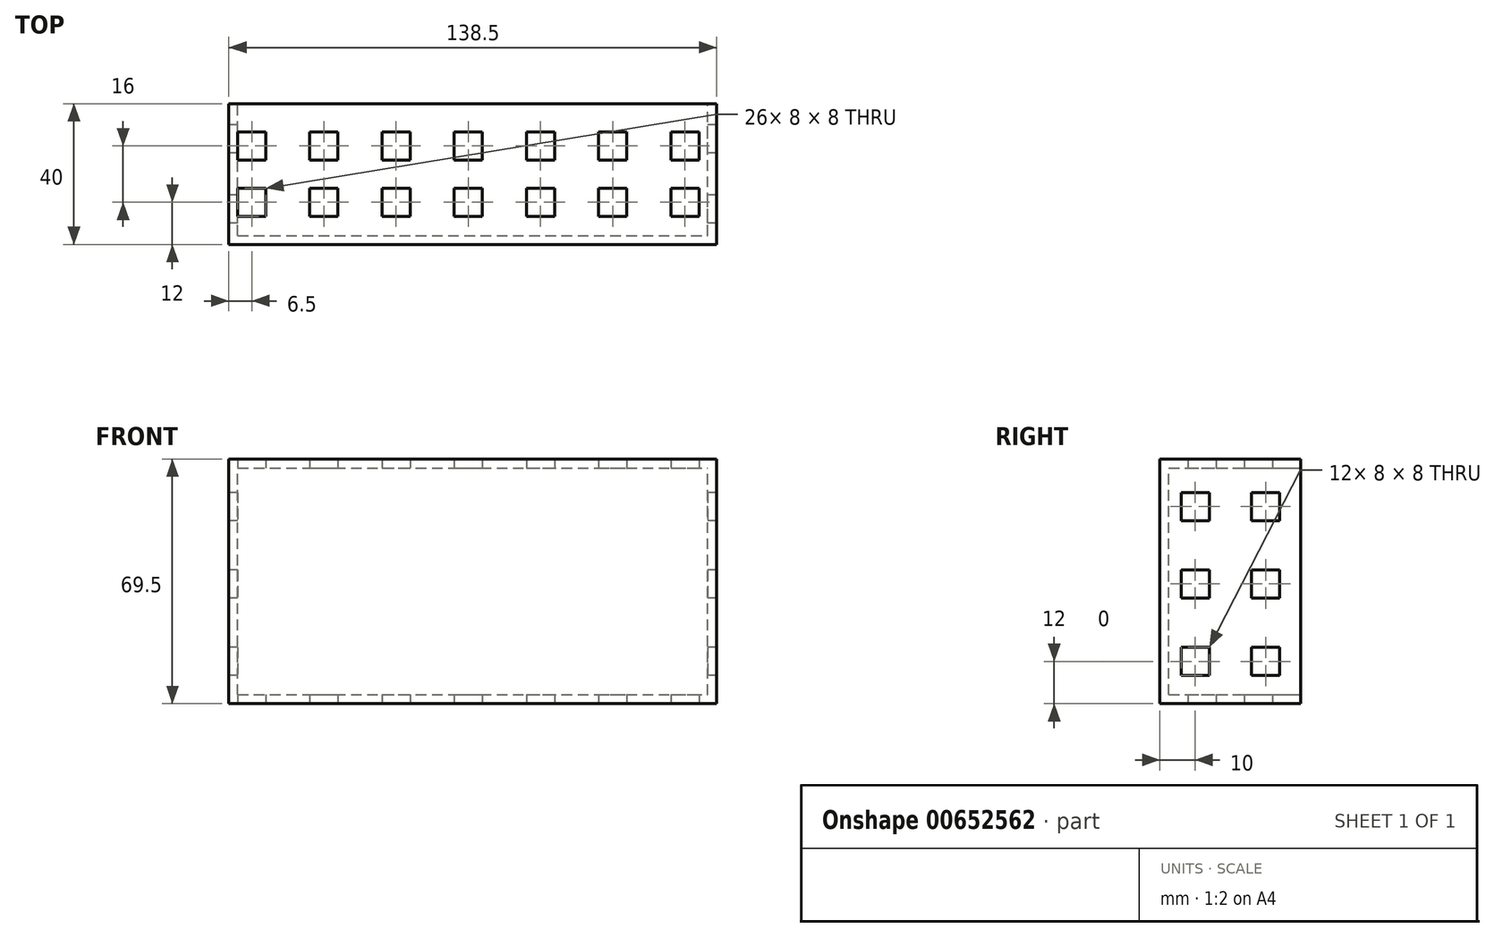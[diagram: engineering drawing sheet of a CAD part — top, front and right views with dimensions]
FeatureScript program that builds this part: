
annotation { "Feature Type Name" : "Feature", "Feature Type Description" : "" }
export const myFeature = defineFeature(function(context is Context, id is Id, definition is map)
    precondition{}
    {
        {
            var Q0;
            Q0=qCreatedBy(makeId("Front.planeOp"),FACE);
            var sketch = newSketch(context, id + "F0", { "sketchPlane" : qUnion([Q0])});
            skLineSegment(sketch, "E0.bottom", {"start": v(0, 0) * mm, "end": v(138.5, 0) * mm});
            skLineSegment(sketch, "E0.top", {"start": v(0, 69.5) * mm, "end": v(138.5, 69.5) * mm});
            skLineSegment(sketch, "E0.left", {"start": v(0, 0) * mm, "end": v(0, 69.5) * mm});
            skLineSegment(sketch, "E0.right", {"start": v(138.5, 0) * mm, "end": v(138.5, 69.5) * mm});
            skSolve(sketch);
        }
        {
            var Q0;
            Q0 = qSketchRegion(id + "F0", true);
            extrude(context, id + "F1", {"entities" : qUnion([Q0]), "depth" : 40 * mm, "offsetDistance" : 25 * mm});
        }
        {
            var Q0;
            Q0=makeQuery(id+"F1.opExtrude","CAP_FACE",FACE,{"disambiguationData":[OSD([sQuery(id+"F0.wireOp",EDGE,"E0.bottom"),sQuery(id+"F0.wireOp",EDGE,"E0.top"),sQuery(id+"F0.wireOp",EDGE,"E0.left"),sQuery(id+"F0.wireOp",EDGE,"E0.right")])],"isStart":true});
            shell(context, id + "F2", {"entities" : qUnion([Q0]), "thickness" : 2.5 * mm});
        }
        {
            var Q0;
            Q0=makeQuery(id+"F1.opExtrude","SWEPT_FACE",FACE,{"disambiguationData":[OSD([sQuery(id+"F0.wireOp",EDGE,"E0.bottom")])]});
            var sketch = newSketch(context, id + "F3", { "sketchPlane" : qUnion([Q0])});
            skLineSegment(sketch, "E1.bottom", {"start": v(10.5, 24) * mm, "end": v(2.5, 24) * mm});
            skLineSegment(sketch, "E1.top", {"start": v(10.5, 32) * mm, "end": v(2.5, 32) * mm});
            skLineSegment(sketch, "E1.left", {"start": v(10.5, 24) * mm, "end": v(10.5, 32) * mm});
            skLineSegment(sketch, "E1.right", {"start": v(2.5, 24) * mm, "end": v(2.5, 32) * mm});
            skPoint(sketch, "E1.middle", {"position": v(6.5, 28) * mm});
            skLineSegment(sketch, "E2.1.0.0", {"start": v(31, 32) * mm, "end": v(23, 32) * mm});
            skLineSegment(sketch, "E2.1.0.1", {"start": v(31, 24) * mm, "end": v(31, 32) * mm});
            skLineSegment(sketch, "E2.1.0.2", {"start": v(31, 24) * mm, "end": v(23, 24) * mm});
            skLineSegment(sketch, "E2.1.0.3", {"start": v(23, 24) * mm, "end": v(23, 32) * mm});
            skLineSegment(sketch, "E2.2.0.0", {"start": v(51.5, 32) * mm, "end": v(43.5, 32) * mm});
            skLineSegment(sketch, "E2.2.0.1", {"start": v(51.5, 24) * mm, "end": v(51.5, 32) * mm});
            skLineSegment(sketch, "E2.2.0.2", {"start": v(51.5, 24) * mm, "end": v(43.5, 24) * mm});
            skLineSegment(sketch, "E2.2.0.3", {"start": v(43.5, 24) * mm, "end": v(43.5, 32) * mm});
            skLineSegment(sketch, "E2.3.0.0", {"start": v(72, 32) * mm, "end": v(64, 32) * mm});
            skLineSegment(sketch, "E2.3.0.1", {"start": v(72, 24) * mm, "end": v(72, 32) * mm});
            skLineSegment(sketch, "E2.3.0.2", {"start": v(72, 24) * mm, "end": v(64, 24) * mm});
            skLineSegment(sketch, "E2.3.0.3", {"start": v(64, 24) * mm, "end": v(64, 32) * mm});
            skLineSegment(sketch, "E2.4.0.0", {"start": v(92.5, 32) * mm, "end": v(84.5, 32) * mm});
            skLineSegment(sketch, "E2.4.0.1", {"start": v(92.5, 24) * mm, "end": v(92.5, 32) * mm});
            skLineSegment(sketch, "E2.4.0.2", {"start": v(92.5, 24) * mm, "end": v(84.5, 24) * mm});
            skLineSegment(sketch, "E2.4.0.3", {"start": v(84.5, 24) * mm, "end": v(84.5, 32) * mm});
            skLineSegment(sketch, "E2.5.0.0", {"start": v(113, 32) * mm, "end": v(105, 32) * mm});
            skLineSegment(sketch, "E2.5.0.1", {"start": v(113, 24) * mm, "end": v(113, 32) * mm});
            skLineSegment(sketch, "E2.5.0.2", {"start": v(113, 24) * mm, "end": v(105, 24) * mm});
            skLineSegment(sketch, "E2.5.0.3", {"start": v(105, 24) * mm, "end": v(105, 32) * mm});
            skLineSegment(sketch, "E2.6.0.0", {"start": v(133.5, 32) * mm, "end": v(125.5, 32) * mm});
            skLineSegment(sketch, "E2.6.0.1", {"start": v(133.5, 24) * mm, "end": v(133.5, 32) * mm});
            skLineSegment(sketch, "E2.6.0.2", {"start": v(133.5, 24) * mm, "end": v(125.5, 24) * mm});
            skLineSegment(sketch, "E2.6.0.3", {"start": v(125.5, 24) * mm, "end": v(125.5, 32) * mm});
            skLineSegment(sketch, "E2.direction1", {"start": v(2.5, 32) * mm, "end": v(23, 32) * mm, "construction": true});
            skLineSegment(sketch, "E3.bottom", {"start": v(10.5, 8) * mm, "end": v(2.5, 8) * mm});
            skLineSegment(sketch, "E3.top", {"start": v(10.5, 16) * mm, "end": v(2.5, 16) * mm});
            skLineSegment(sketch, "E3.left", {"start": v(10.5, 8) * mm, "end": v(10.5, 16) * mm});
            skLineSegment(sketch, "E3.right", {"start": v(2.5, 8) * mm, "end": v(2.5, 16) * mm});
            skPoint(sketch, "E3.middle", {"position": v(6.5, 12) * mm});
            skLineSegment(sketch, "E4.1.0.0", {"start": v(31, 16) * mm, "end": v(23, 16) * mm});
            skLineSegment(sketch, "E4.1.0.1", {"start": v(31, 8) * mm, "end": v(31, 16) * mm});
            skLineSegment(sketch, "E4.1.0.2", {"start": v(31, 8) * mm, "end": v(23, 8) * mm});
            skLineSegment(sketch, "E4.1.0.3", {"start": v(23, 8) * mm, "end": v(23, 16) * mm});
            skLineSegment(sketch, "E4.2.0.0", {"start": v(51.5, 16) * mm, "end": v(43.5, 16) * mm});
            skLineSegment(sketch, "E4.2.0.1", {"start": v(51.5, 8) * mm, "end": v(51.5, 16) * mm});
            skLineSegment(sketch, "E4.2.0.2", {"start": v(51.5, 8) * mm, "end": v(43.5, 8) * mm});
            skLineSegment(sketch, "E4.2.0.3", {"start": v(43.5, 8) * mm, "end": v(43.5, 16) * mm});
            skLineSegment(sketch, "E4.3.0.0", {"start": v(72, 16) * mm, "end": v(64, 16) * mm});
            skLineSegment(sketch, "E4.3.0.1", {"start": v(72, 8) * mm, "end": v(72, 16) * mm});
            skLineSegment(sketch, "E4.3.0.2", {"start": v(72, 8) * mm, "end": v(64, 8) * mm});
            skLineSegment(sketch, "E4.3.0.3", {"start": v(64, 8) * mm, "end": v(64, 16) * mm});
            skLineSegment(sketch, "E4.4.0.0", {"start": v(92.5, 16) * mm, "end": v(84.5, 16) * mm});
            skLineSegment(sketch, "E4.4.0.1", {"start": v(92.5, 8) * mm, "end": v(92.5, 16) * mm});
            skLineSegment(sketch, "E4.4.0.2", {"start": v(92.5, 8) * mm, "end": v(84.5, 8) * mm});
            skLineSegment(sketch, "E4.4.0.3", {"start": v(84.5, 8) * mm, "end": v(84.5, 16) * mm});
            skLineSegment(sketch, "E4.5.0.0", {"start": v(113, 16) * mm, "end": v(105, 16) * mm});
            skLineSegment(sketch, "E4.5.0.1", {"start": v(113, 8) * mm, "end": v(113, 16) * mm});
            skLineSegment(sketch, "E4.5.0.2", {"start": v(113, 8) * mm, "end": v(105, 8) * mm});
            skLineSegment(sketch, "E4.5.0.3", {"start": v(105, 8) * mm, "end": v(105, 16) * mm});
            skLineSegment(sketch, "E4.6.0.0", {"start": v(133.5, 16) * mm, "end": v(125.5, 16) * mm});
            skLineSegment(sketch, "E4.6.0.1", {"start": v(133.5, 8) * mm, "end": v(133.5, 16) * mm});
            skLineSegment(sketch, "E4.6.0.2", {"start": v(133.5, 8) * mm, "end": v(125.5, 8) * mm});
            skLineSegment(sketch, "E4.6.0.3", {"start": v(125.5, 8) * mm, "end": v(125.5, 16) * mm});
            skLineSegment(sketch, "E4.direction1", {"start": v(2.5, 16) * mm, "end": v(23, 16) * mm, "construction": true});
            skSolve(sketch);
        }
        {
            var Q0;
            Q0=makeQuery(id+"F3.imprint","IMPRINT",FACE,{"disambiguationData":[TD([[makeQuery(id+"F3.imprint","IMPRINT",EDGE,{"derivedFrom":sQuery(id+"F3.wireOp",EDGE,"E1.bottom")}),-1.0]])]});
            var Q1;
            Q1=makeQuery(id+"F3.imprint","IMPRINT",FACE,{"disambiguationData":[TD([[makeQuery(id+"F3.imprint","IMPRINT",EDGE,{"derivedFrom":sQuery(id+"F3.wireOp",EDGE,"E2.1.0.0")}),1.0]])]});
            var Q2;
            Q2=makeQuery(id+"F3.imprint","IMPRINT",FACE,{"disambiguationData":[TD([[makeQuery(id+"F3.imprint","IMPRINT",EDGE,{"derivedFrom":sQuery(id+"F3.wireOp",EDGE,"E4.1.0.0")}),1.0]])]});
            var Q3;
            Q3=makeQuery(id+"F3.imprint","IMPRINT",FACE,{"disambiguationData":[TD([[makeQuery(id+"F3.imprint","IMPRINT",EDGE,{"derivedFrom":sQuery(id+"F3.wireOp",EDGE,"E3.bottom")}),-1.0]])]});
            var Q4;
            Q4=makeQuery(id+"F3.imprint","IMPRINT",FACE,{"disambiguationData":[TD([[makeQuery(id+"F3.imprint","IMPRINT",EDGE,{"derivedFrom":sQuery(id+"F3.wireOp",EDGE,"E4.2.0.0")}),1.0]])]});
            var Q5;
            Q5=makeQuery(id+"F3.imprint","IMPRINT",FACE,{"disambiguationData":[TD([[makeQuery(id+"F3.imprint","IMPRINT",EDGE,{"derivedFrom":sQuery(id+"F3.wireOp",EDGE,"E2.2.0.0")}),1.0]])]});
            var Q6;
            Q6=makeQuery(id+"F3.imprint","IMPRINT",FACE,{"disambiguationData":[TD([[makeQuery(id+"F3.imprint","IMPRINT",EDGE,{"derivedFrom":sQuery(id+"F3.wireOp",EDGE,"E2.3.0.0")}),1.0]])]});
            var Q7;
            Q7=makeQuery(id+"F3.imprint","IMPRINT",FACE,{"disambiguationData":[TD([[makeQuery(id+"F3.imprint","IMPRINT",EDGE,{"derivedFrom":sQuery(id+"F3.wireOp",EDGE,"E4.3.0.0")}),1.0]])]});
            var Q8;
            Q8=makeQuery(id+"F3.imprint","IMPRINT",FACE,{"disambiguationData":[TD([[makeQuery(id+"F3.imprint","IMPRINT",EDGE,{"derivedFrom":sQuery(id+"F3.wireOp",EDGE,"E4.4.0.0")}),1.0]])]});
            var Q9;
            Q9=makeQuery(id+"F3.imprint","IMPRINT",FACE,{"disambiguationData":[TD([[makeQuery(id+"F3.imprint","IMPRINT",EDGE,{"derivedFrom":sQuery(id+"F3.wireOp",EDGE,"E2.4.0.0")}),1.0]])]});
            var Q10;
            Q10=makeQuery(id+"F3.imprint","IMPRINT",FACE,{"disambiguationData":[TD([[makeQuery(id+"F3.imprint","IMPRINT",EDGE,{"derivedFrom":sQuery(id+"F3.wireOp",EDGE,"E2.5.0.0")}),1.0]])]});
            var Q11;
            Q11=makeQuery(id+"F3.imprint","IMPRINT",FACE,{"disambiguationData":[TD([[makeQuery(id+"F3.imprint","IMPRINT",EDGE,{"derivedFrom":sQuery(id+"F3.wireOp",EDGE,"E4.5.0.0")}),1.0]])]});
            var Q12;
            Q12=makeQuery(id+"F3.imprint","IMPRINT",FACE,{"disambiguationData":[TD([[makeQuery(id+"F3.imprint","IMPRINT",EDGE,{"derivedFrom":sQuery(id+"F3.wireOp",EDGE,"E4.6.0.0")}),1.0]])]});
            var Q13;
            Q13=makeQuery(id+"F3.imprint","IMPRINT",FACE,{"disambiguationData":[TD([[makeQuery(id+"F3.imprint","IMPRINT",EDGE,{"derivedFrom":sQuery(id+"F3.wireOp",EDGE,"E2.6.0.0")}),1.0]])]});
            extrude(context, id + "F4", {"entities" : qUnion([Q0, Q1, Q2, Q3, Q4, Q5, Q6, Q7, Q8, Q9, Q10, Q11, Q12, Q13]), "operationType" : NewBodyOperationType.REMOVE, "oppositeDirection" : true, "depth" : 100 * mm, "offsetDistance" : 25 * mm});
        }
        {
            var Q0;
            Q0=makeQuery(id+"F1.opExtrude","SWEPT_FACE",FACE,{"disambiguationData":[OSD([sQuery(id+"F0.wireOp",EDGE,"E0.left")])]});
            var sketch = newSketch(context, id + "F5", { "sketchPlane" : qUnion([Q0])});
            skLineSegment(sketch, "E5.bottom", {"start": v(14, 16) * mm, "end": v(6, 16) * mm});
            skLineSegment(sketch, "E5.top", {"start": v(14, 8) * mm, "end": v(6, 8) * mm});
            skLineSegment(sketch, "E5.left", {"start": v(14, 16) * mm, "end": v(14, 8) * mm});
            skLineSegment(sketch, "E5.right", {"start": v(6, 16) * mm, "end": v(6, 8) * mm});
            skPoint(sketch, "E5.middle", {"position": v(10, 12) * mm});
            skLineSegment(sketch, "E6.0.1.0", {"start": v(14, 30) * mm, "end": v(6, 30) * mm});
            skLineSegment(sketch, "E6.0.1.1", {"start": v(14, 38) * mm, "end": v(14, 30) * mm});
            skLineSegment(sketch, "E6.0.1.2", {"start": v(14, 38) * mm, "end": v(6, 38) * mm});
            skLineSegment(sketch, "E6.0.1.3", {"start": v(6, 38) * mm, "end": v(6, 30) * mm});
            skLineSegment(sketch, "E6.0.2.0", {"start": v(14, 52) * mm, "end": v(6, 52) * mm});
            skLineSegment(sketch, "E6.0.2.1", {"start": v(14, 60) * mm, "end": v(14, 52) * mm});
            skLineSegment(sketch, "E6.0.2.2", {"start": v(14, 60) * mm, "end": v(6, 60) * mm});
            skLineSegment(sketch, "E6.0.2.3", {"start": v(6, 60) * mm, "end": v(6, 52) * mm});
            skLineSegment(sketch, "E6.1.0.0", {"start": v(34, 8) * mm, "end": v(26, 8) * mm});
            skLineSegment(sketch, "E6.1.0.1", {"start": v(34, 16) * mm, "end": v(34, 8) * mm});
            skLineSegment(sketch, "E6.1.0.2", {"start": v(34, 16) * mm, "end": v(26, 16) * mm});
            skLineSegment(sketch, "E6.1.0.3", {"start": v(26, 16) * mm, "end": v(26, 8) * mm});
            skLineSegment(sketch, "E6.1.1.0", {"start": v(34, 30) * mm, "end": v(26, 30) * mm});
            skLineSegment(sketch, "E6.1.1.1", {"start": v(34, 38) * mm, "end": v(34, 30) * mm});
            skLineSegment(sketch, "E6.1.1.2", {"start": v(34, 38) * mm, "end": v(26, 38) * mm});
            skLineSegment(sketch, "E6.1.1.3", {"start": v(26, 38) * mm, "end": v(26, 30) * mm});
            skLineSegment(sketch, "E6.1.2.0", {"start": v(34, 52) * mm, "end": v(26, 52) * mm});
            skLineSegment(sketch, "E6.1.2.1", {"start": v(34, 60) * mm, "end": v(34, 52) * mm});
            skLineSegment(sketch, "E6.1.2.2", {"start": v(34, 60) * mm, "end": v(26, 60) * mm});
            skLineSegment(sketch, "E6.1.2.3", {"start": v(26, 60) * mm, "end": v(26, 52) * mm});
            skLineSegment(sketch, "E6.direction1", {"start": v(6, 8) * mm, "end": v(26, 8) * mm, "construction": true});
            skLineSegment(sketch, "E6.direction2", {"start": v(6, 8) * mm, "end": v(6, 30) * mm, "construction": true});
            skSolve(sketch);
        }
        {
            var Q0;
            Q0=makeQuery(id+"F5.imprint","IMPRINT",FACE,{"disambiguationData":[TD([[makeQuery(id+"F5.imprint","IMPRINT",EDGE,{"derivedFrom":sQuery(id+"F5.wireOp",EDGE,"E5.bottom")}),1.0]])]});
            var Q1;
            Q1=makeQuery(id+"F5.imprint","IMPRINT",FACE,{"disambiguationData":[TD([[makeQuery(id+"F5.imprint","IMPRINT",EDGE,{"derivedFrom":sQuery(id+"F5.wireOp",EDGE,"E6.0.1.0")}),-1.0]])]});
            var Q2;
            Q2=makeQuery(id+"F5.imprint","IMPRINT",FACE,{"disambiguationData":[TD([[makeQuery(id+"F5.imprint","IMPRINT",EDGE,{"derivedFrom":sQuery(id+"F5.wireOp",EDGE,"E6.1.0.0")}),-1.0]])]});
            var Q3;
            Q3=makeQuery(id+"F5.imprint","IMPRINT",FACE,{"disambiguationData":[TD([[makeQuery(id+"F5.imprint","IMPRINT",EDGE,{"derivedFrom":sQuery(id+"F5.wireOp",EDGE,"E6.1.1.0")}),-1.0]])]});
            var Q4;
            Q4=makeQuery(id+"F5.imprint","IMPRINT",FACE,{"disambiguationData":[TD([[makeQuery(id+"F5.imprint","IMPRINT",EDGE,{"derivedFrom":sQuery(id+"F5.wireOp",EDGE,"E6.1.2.0")}),-1.0]])]});
            var Q5;
            Q5=makeQuery(id+"F5.imprint","IMPRINT",FACE,{"disambiguationData":[TD([[makeQuery(id+"F5.imprint","IMPRINT",EDGE,{"derivedFrom":sQuery(id+"F5.wireOp",EDGE,"E6.0.2.0")}),-1.0]])]});
            extrude(context, id + "F6", {"entities" : qUnion([Q0, Q1, Q2, Q3, Q4, Q5]), "operationType" : NewBodyOperationType.REMOVE, "oppositeDirection" : true, "depth" : 200 * mm, "offsetDistance" : 25 * mm});
        }
    });
